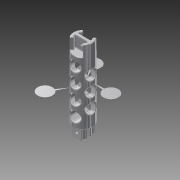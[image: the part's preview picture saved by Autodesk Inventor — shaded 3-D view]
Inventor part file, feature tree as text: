
AUTODESK INVENTOR PART (.ipt)
format: ipt  version: 2014 (Build 180170000, 170)  size: 871,936 bytes
history: native  units: mm
features: extrude x8, sketch x5, plane x3, other x2, mirror x2, fillet x2, folder x1
ambient origin geometry x8: Origin, YZ Plane, XZ Plane, XY Plane, X Axis, Y Axis, Z Axis, Center Point
bodies: Solid1 (feature_tree)
feature tree (23):
  folder  "Master Lengths"
  other  "Profile"
  extrude  "Plug Side"  Depth=2.0mm
  extrude  "Fuse Section"  TaperAngle=45.0deg  [1 undecoded]
  plane  "Work Plane2"
  extrude  "Clamp Side Extrude"  Depth=15.0mm TaperAngle=0.0deg
  mirror  "Mirror2"
  fillet  "Fillet1"  Radius=85.0mm
  extrude  "Extrusion4"  Depth=12.0mm
  extrude  "Extrusion5"  Depth=0.6mm
  fillet  "Fillet4"  Radius=15.0mm
  extrude  "Extrusion6"  Depth=0.6mm
  plane  "Work Plane3"
  plane  "Work Plane4"
  sketch  "Sketch7"  dims[d11=0.0mm d12=12.0mm]
  sketch  "Sketch8"  dims[d13=12.0mm d14=15.0mm d16=15.0mm d18=100.0mm d19=25.0mm d21=85.0mm d23=-85.0mm d24=15.0mm d25=0.0mm d26=1.0mm d27=1.0mm d28=6.0mm d29=0.0mm d32=40.0mm d33=0.0mm d37=0.0mm d41=14.0mm d42=14.0mm d43=12.8mm d44=85.0mm d45=12.8mm d47=14.0mm d49=22.7mm d50=22.7mm d51=40.0mm d52=0.0mm d54=4.0mm d56=4.0mm d57=7.5mm d58=7.5mm d59=7.5mm d60=7.5mm d61=0.0mm d62=0.0mm d63=20.0mm d64=0.0mm d65=14.0mm d66=14.0mm d67=19.8mm d68=19.8mm d69=14.0mm d70=14.0mm d71=2.9mm d72=2.9mm d73=2.9mm d74=2.9mm d75=1.0mm d76=26.0mm d77=-32.75mm d78=-42.5mm d79=26.0mm d80=1.570796mm d81=0.785398mm d82=15.0mm d83=15.0mm d84=10.0mm d85=26.0mm d86=120.0deg d87=120.0deg d88=1.570796mm d89=0.785398mm d90=15.0mm d91=10.0mm d92=0.6mm d93=0.0mm d94=0.6mm d95=0.0mm d96=26.0mm d97=4.0mm d98=2.0mm d99=2.0mm d100=45.0deg d101=0.5mm d102=0.5mm d103=0.5mm d104=0.5mm d105=0.2mm d106=0.2mm d107=0.4mm d108=0.4mm d109=0.2mm d110=0.4mm d111=0.4mm]
  extrude  "Extrusion7"  Depth=0.6mm
  extrude  "Extrusion8"  Depth=0.6mm
  mirror  "Mirror1"
  other  "Clamp Side"
  sketch  "Sketch4"  dims[d0=4.0mm d2=2.0mm]
  sketch  "Sketch5"  dims[d4=4.0mm d5=45.0deg]
  sketch  "Sketch6"  dims[d6=45.0deg d7=15.0mm d8=0.0mm d9=85.0mm d10=0.0mm]
note: 1 required parameter value undecoded (feature->parameter linkage not recoverable at this tier; creation-order binding heuristic only, values carry confidence <= 0.55)
